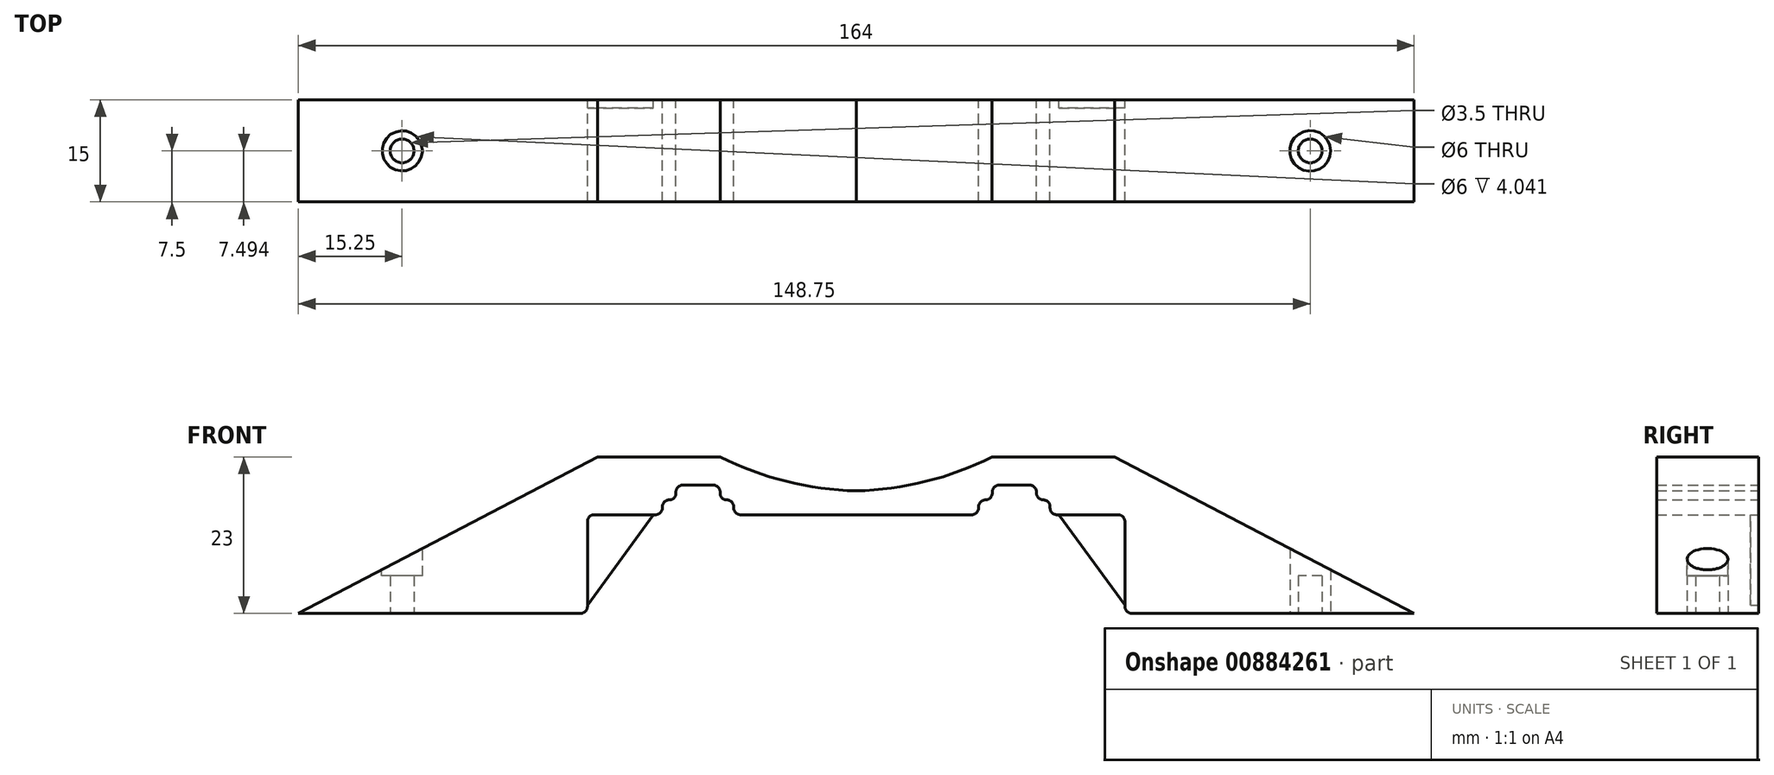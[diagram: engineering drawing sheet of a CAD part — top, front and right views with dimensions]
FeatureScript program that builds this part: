
annotation { "Feature Type Name" : "Feature", "Feature Type Description" : "" }
export const myFeature = defineFeature(function(context is Context, id is Id, definition is map)
    precondition{}
    {
        {
            var Q0;
            Q0=qCreatedBy(makeId("Top.planeOp"),FACE);
            cPlane(context, id + "F0", {"entities" : qUnion([Q0]), "cplaneType" : CPlaneType.OFFSET, "offset" : 10 * mm, "width" : 150 * mm, "height" : 150 * mm});
        }
        {
            var Q0;
            Q0=qCreatedBy(makeId("Front.planeOp"),FACE);
            var sketch = newSketch(context, id + "F1", { "sketchPlane" : qUnion([Q0])});
            skLineSegment(sketch, "E0", {"start": v(0, 122.54) * mm, "end": v(0, -122.54) * mm, "construction": true});
            skLineSegment(sketch, "E1", {"start": v(-40.5, 0) * mm, "end": v(-82, 0) * mm});
            skLineSegment(sketch, "E2", {"start": v(0, 0) * mm, "end": v(0, 14.5) * mm});
            skLineSegment(sketch, "E3", {"start": v(-19.97, 23) * mm, "end": v(-38, 23) * mm});
            skLineSegment(sketch, "E4", {"start": v(-38, 23) * mm, "end": v(-82, 0) * mm});
            skLineSegment(sketch, "E5.top", {"start": v(0, 14.5) * mm, "end": v(-17, 14.5) * mm});
            skLineSegment(sketch, "E5.right", {"start": v(-39.5, 1) * mm, "end": v(-39.5, 13.5) * mm});
            skLineSegment(sketch, "E6.0", {"start": v(-20, 122.54) * mm, "end": v(-20, 18.86) * mm, "construction": true});
            skLineSegment(sketch, "E7.top", {"start": v(-21, 18.86) * mm, "end": v(-25.5, 18.86) * mm});
            skLineSegment(sketch, "E7.left", {"start": v(-20, 14.5) * mm, "end": v(-20, 16.68) * mm});
            skLineSegment(sketch, "E7.right", {"start": v(-26.5, 17.68) * mm, "end": v(-26.5, 17.86) * mm});
            skLineSegment(sketch, "E8.trimOffspring", {"start": v(-29.5, 14.5) * mm, "end": v(-38.5, 14.5) * mm});
            skLineSegment(sketch, "E9.MirrorCS", {"start": v(19.97, 23) * mm, "end": v(38, 23) * mm});
            skLineSegment(sketch, "E10.MirrorCS", {"start": v(38, 23) * mm, "end": v(82, 0) * mm});
            skLineSegment(sketch, "E11.MirrorCS", {"start": v(40.5, 0) * mm, "end": v(82, 0) * mm});
            skLineSegment(sketch, "E12.MirrorCS", {"start": v(39.5, 1) * mm, "end": v(39.5, 13.5) * mm});
            skLineSegment(sketch, "E13.MirrorCS", {"start": v(29.5, 14.5) * mm, "end": v(38.5, 14.5) * mm});
            skLineSegment(sketch, "E14.MirrorCS", {"start": v(21, 18.86) * mm, "end": v(25.5, 18.86) * mm});
            skLineSegment(sketch, "E15.MirrorCS", {"start": v(0, 14.5) * mm, "end": v(17, 14.5) * mm});
            skLineSegment(sketch, "E16.MirrorCS", {"start": v(20, 17.68) * mm, "end": v(20, 17.86) * mm});
            skLineSegment(sketch, "E17.MirrorCS", {"start": v(26.5, 17.68) * mm, "end": v(26.5, 17.86) * mm});
            skPoint(sketch, "E18.oppositeSnap0", {"position": v(-20, 16.68) * mm});
            skLineSegment(sketch, "E18.top", {"start": v(-27.5, 16.68) * mm, "end": v(-27.5, 16.68) * mm});
            skLineSegment(sketch, "E18.left", {"start": v(-28.5, 15.5) * mm, "end": v(-28.5, 15.68) * mm});
            skLineSegment(sketch, "E18.right", {"start": v(-18, 15.5) * mm, "end": v(-18, 15.68) * mm});
            skLineSegment(sketch, "E19.trimOffspring", {"start": v(-19, 16.68) * mm, "end": v(-19, 16.68) * mm});
            skPoint(sketch, "E20.orphan", {"position": v(-26.5, 14.5) * mm});
            skLineSegment(sketch, "E21.trimOffspring", {"start": v(-20, 14.5) * mm, "end": v(-20, -122.54) * mm, "construction": true});
            skLineSegment(sketch, "E22.MirrorCS", {"start": v(27.5, 16.68) * mm, "end": v(27.5, 16.68) * mm});
            skLineSegment(sketch, "E23.MirrorCS", {"start": v(28.5, 15.5) * mm, "end": v(28.5, 15.68) * mm});
            skLineSegment(sketch, "E24.MirrorCS", {"start": v(19, 16.68) * mm, "end": v(19, 16.68) * mm});
            skLineSegment(sketch, "E25.MirrorCS", {"start": v(18, 15.5) * mm, "end": v(18, 15.68) * mm});
            skPoint(sketch, "E26.orphan", {"position": v(20, 14.5) * mm});
            skPoint(sketch, "E27.orphan", {"position": v(26.5, 14.5) * mm});
            skLineSegment(sketch, "E28.0", {"start": v(-62.24, 18.01) * mm, "end": v(64.94, 18.01) * mm, "construction": true});
            skArc(sketch, "E29", {"start": v(-20, 23.01) * mm, "mid": v(-10.28, 19.4) * mm, "end": v(0, 18.01) * mm});
            skArc(sketch, "E30.MirrorCS", {"start": v(20, 23.01) * mm, "mid": v(10.28, 19.4) * mm, "end": v(0, 18.01) * mm});
            skPoint(sketch, "E31.orphan", {"position": v(0, 23) * mm});
            skPoint(sketch, "E32.visualSharp", {"position": v(-26.5, 18.86) * mm});
            skArc(sketch, "E32.filletArc", {"start": v(-25.5, 18.86) * mm, "mid": v(-26.2, 18.57) * mm, "end": v(-26.5, 17.86) * mm});
            skPoint(sketch, "E33.visualSharp", {"position": v(-28.5, 16.68) * mm});
            skArc(sketch, "E33.filletArc", {"start": v(-27.5, 16.68) * mm, "mid": v(-28.2, 16.39) * mm, "end": v(-28.5, 15.68) * mm});
            skPoint(sketch, "E34.visualSharp", {"position": v(-18, 16.68) * mm});
            skArc(sketch, "E34.filletArc", {"start": v(-18, 15.68) * mm, "mid": v(-18.3, 16.39) * mm, "end": v(-19, 16.68) * mm});
            skLineSegment(sketch, "E35", {"start": v(-20, 17.86) * mm, "end": v(-20, 17.68) * mm});
            skPoint(sketch, "E36.visualSharp", {"position": v(-20, 18.86) * mm});
            skArc(sketch, "E36.filletArc", {"start": v(-20, 17.86) * mm, "mid": v(-20.3, 18.57) * mm, "end": v(-21, 18.86) * mm});
            skPoint(sketch, "E37.visualSharp", {"position": v(-26.5, 16.68) * mm});
            skArc(sketch, "E37.filletArc", {"start": v(-27.5, 16.68) * mm, "mid": v(-26.8, 16.97) * mm, "end": v(-26.5, 17.68) * mm});
            skArc(sketch, "E38.filletArc", {"start": v(-20, 17.68) * mm, "mid": v(-19.7, 16.97) * mm, "end": v(-19, 16.68) * mm});
            skPoint(sketch, "E39.visualSharp", {"position": v(18, 16.68) * mm});
            skArc(sketch, "E39.filletArc", {"start": v(19, 16.68) * mm, "mid": v(18.3, 16.39) * mm, "end": v(18, 15.68) * mm});
            skPoint(sketch, "E40.visualSharp", {"position": v(20, 18.86) * mm});
            skArc(sketch, "E40.filletArc", {"start": v(21, 18.86) * mm, "mid": v(20.3, 18.57) * mm, "end": v(20, 17.86) * mm});
            skPoint(sketch, "E41.visualSharp", {"position": v(26.5, 18.86) * mm});
            skArc(sketch, "E41.filletArc", {"start": v(26.5, 17.86) * mm, "mid": v(26.2, 18.57) * mm, "end": v(25.5, 18.86) * mm});
            skPoint(sketch, "E42.visualSharp", {"position": v(28.5, 16.68) * mm});
            skArc(sketch, "E42.filletArc", {"start": v(28.5, 15.68) * mm, "mid": v(28.2, 16.39) * mm, "end": v(27.5, 16.68) * mm});
            skPoint(sketch, "E43.visualSharp", {"position": v(26.5, 16.68) * mm});
            skArc(sketch, "E43.filletArc", {"start": v(26.5, 17.68) * mm, "mid": v(26.8, 16.97) * mm, "end": v(27.5, 16.68) * mm});
            skPoint(sketch, "E44.visualSharp", {"position": v(20, 16.68) * mm});
            skArc(sketch, "E44.filletArc", {"start": v(19, 16.68) * mm, "mid": v(19.7, 16.97) * mm, "end": v(20, 17.68) * mm});
            skPoint(sketch, "E45.visualSharp", {"position": v(-39.5, 14.5) * mm});
            skArc(sketch, "E45.filletArc", {"start": v(-38.5, 14.5) * mm, "mid": v(-39.2, 14.2) * mm, "end": v(-39.5, 13.5) * mm});
            skPoint(sketch, "E46.visualSharp", {"position": v(-28.5, 14.5) * mm});
            skArc(sketch, "E46.filletArc", {"start": v(-29.5, 14.5) * mm, "mid": v(-28.8, 14.8) * mm, "end": v(-28.5, 15.5) * mm});
            skPoint(sketch, "E47.visualSharp", {"position": v(-18, 14.5) * mm});
            skArc(sketch, "E47.filletArc", {"start": v(-18, 15.5) * mm, "mid": v(-17.7, 14.8) * mm, "end": v(-17, 14.5) * mm});
            skPoint(sketch, "E48.visualSharp", {"position": v(-39.5, 0) * mm});
            skArc(sketch, "E48.filletArc", {"start": v(-40.5, 0) * mm, "mid": v(-39.8, 0.3) * mm, "end": v(-39.5, 1) * mm});
            skPoint(sketch, "E49.visualSharp", {"position": v(18, 14.5) * mm});
            skArc(sketch, "E49.filletArc", {"start": v(17, 14.5) * mm, "mid": v(17.7, 14.8) * mm, "end": v(18, 15.5) * mm});
            skPoint(sketch, "E50.visualSharp", {"position": v(28.5, 14.5) * mm});
            skArc(sketch, "E50.filletArc", {"start": v(28.5, 15.5) * mm, "mid": v(28.8, 14.8) * mm, "end": v(29.5, 14.5) * mm});
            skPoint(sketch, "E51.visualSharp", {"position": v(39.5, 14.5) * mm});
            skArc(sketch, "E51.filletArc", {"start": v(39.5, 13.5) * mm, "mid": v(39.2, 14.2) * mm, "end": v(38.5, 14.5) * mm});
            skPoint(sketch, "E52.visualSharp", {"position": v(39.5, 0) * mm});
            skArc(sketch, "E52.filletArc", {"start": v(39.5, 1) * mm, "mid": v(39.8, 0.3) * mm, "end": v(40.5, 0) * mm});
            skSolve(sketch);
        }
        {
            var Q0;
            Q0=makeQuery(id+"F1.imprint","IMPRINT",FACE,{"disambiguationData":[TD([[makeQuery(id+"F1.imprint","IMPRINT",EDGE,{"derivedFrom":sQuery(id+"F1.wireOp",EDGE,"E1")}),-1.0]])]});
            extrude(context, id + "F2", {"entities" : qUnion([Q0]), "depth" : 15 * mm, "offsetDistance" : 25 * mm});
        }
        {
            var Q0;
            Q0=qCreatedBy(makeId("Top.planeOp"),FACE);
            var sketch = newSketch(context, id + "F3", { "sketchPlane" : qUnion([Q0])});
            skLineSegment(sketch, "E53", {"start": v(0, 0) * mm, "end": v(-3.58, 0) * mm, "construction": true});
            skLineSegment(sketch, "E54", {"start": v(-109.94, 0) * mm, "end": v(106.23, 0) * mm, "construction": true});
            skLineSegment(sketch, "E55.0", {"start": v(-109.94, -7.5) * mm, "end": v(106.23, -7.5) * mm, "construction": true});
            skLineSegment(sketch, "E56", {"start": v(-82, -15) * mm, "end": v(-82, 17.83) * mm, "construction": true});
            skLineSegment(sketch, "E57.0", {"start": v(-66.75, -15) * mm, "end": v(-66.75, 17.83) * mm, "construction": true});
            skCircle(sketch, "E58", {"center": v(-66.75, -7.5) * mm, "radius": 1.75 * mm});
            skLineSegment(sketch, "E59", {"start": v(0, 23.95) * mm, "end": v(0, -38.43) * mm, "construction": true});
            skCircle(sketch, "E60.MirrorC", {"center": v(66.75, -7.5) * mm, "radius": 1.75 * mm});
            skCircle(sketch, "E61", {"center": v(-66.75, -7.5) * mm, "radius": 3 * mm});
            skCircle(sketch, "E62.MirrorC", {"center": v(66.75, -7.5) * mm, "radius": 3 * mm});
            skSolve(sketch);
        }
        {
            var Q0;
            Q0=makeQuery(id+"F3.imprint","IMPRINT",FACE,{"disambiguationData":[TD([[makeQuery(id+"F3.imprint","IMPRINT",EDGE,{"derivedFrom":sQuery(id+"F3.wireOp",EDGE,"E60.MirrorC")}),-1.0]])]});
            var Q1;
            Q1=makeQuery(id+"F3.imprint","IMPRINT",FACE,{"disambiguationData":[TD([[makeQuery(id+"F3.imprint","IMPRINT",EDGE,{"derivedFrom":sQuery(id+"F3.wireOp",EDGE,"E58")}),1.0]])]});
            extrude(context, id + "F4", {"entities" : qUnion([Q0, Q1]), "operationType" : NewBodyOperationType.REMOVE, "endBound" : BoundingType.THROUGH_ALL, "depth" : 25 * mm, "offsetDistance" : 25 * mm});
        }
        {
            var Q0;
            Q0=qCreatedBy(id+"F0.planeOp",FACE);
            var sketch = newSketch(context, id + "F5", { "sketchPlane" : qUnion([Q0])});
            skCircle(sketch, "E63", {"center": v(-66.75, -7.5) * mm, "radius": 3 * mm});
            skCircle(sketch, "E64", {"center": v(66.75, -7.5) * mm, "radius": 3 * mm});
            skSolve(sketch);
        }
        {
            var Q0;
            Q0=makeQuery(id+"F5.imprint","IMPRINT",FACE,{"disambiguationData":[TD([[makeQuery(id+"F5.imprint","IMPRINT",EDGE,{"derivedFrom":sQuery(id+"F5.wireOp",EDGE,"E63")}),1.0]])]});
            var Q1;
            Q1=makeQuery(id+"F5.imprint","IMPRINT",FACE,{"disambiguationData":[TD([[makeQuery(id+"F5.imprint","IMPRINT",EDGE,{"derivedFrom":sQuery(id+"F5.wireOp",EDGE,"E64")}),1.0]])]});
            extrude(context, id + "F6", {"entities" : qUnion([Q0, Q1]), "operationType" : NewBodyOperationType.REMOVE, "oppositeDirection" : true, "depth" : 4.5 * mm, "offsetDistance" : 25 * mm});
        }
        {
            var Q0;
            Q0=qCreatedBy(makeId("Front.planeOp"),FACE);
            var sketch = newSketch(context, id + "F7", { "sketchPlane" : qUnion([Q0])});
            skLineSegment(sketch, "E65", {"start": v(-39.5, 1.22) * mm, "end": v(-29.83, 14.5) * mm});
            skLineSegment(sketch, "E66", {"start": v(-29.83, 14.5) * mm, "end": v(-38.5, 14.5) * mm});
            skLineSegment(sketch, "E67", {"start": v(-39.5, 13.5) * mm, "end": v(-39.5, 1.22) * mm});
            skPoint(sketch, "E68.visualSharp", {"position": v(-39.5, 14.5) * mm});
            skArc(sketch, "E68.filletArc", {"start": v(-38.5, 14.5) * mm, "mid": v(-39.2, 14.2) * mm, "end": v(-39.5, 13.5) * mm});
            skLineSegment(sketch, "E69.MirrorCS", {"start": v(39.5, 1.22) * mm, "end": v(29.83, 14.5) * mm});
            skLineSegment(sketch, "E70.MirrorCS", {"start": v(29.83, 14.5) * mm, "end": v(38.5, 14.5) * mm});
            skLineSegment(sketch, "E71.MirrorCS", {"start": v(39.5, 13.5) * mm, "end": v(39.5, 1.22) * mm});
            skArc(sketch, "E72.MirrorCS", {"start": v(38.5, 14.5) * mm, "mid": v(39.2, 14.2) * mm, "end": v(39.5, 13.5) * mm});
            skSolve(sketch);
        }
        {
            var Q0;
            Q0 = qSketchRegion(id + "F7", true);
            extrude(context, id + "F8", {"entities" : qUnion([Q0]), "operationType" : NewBodyOperationType.ADD, "depth" : 1.2 * mm, "offsetDistance" : 25 * mm});
        }
    });
